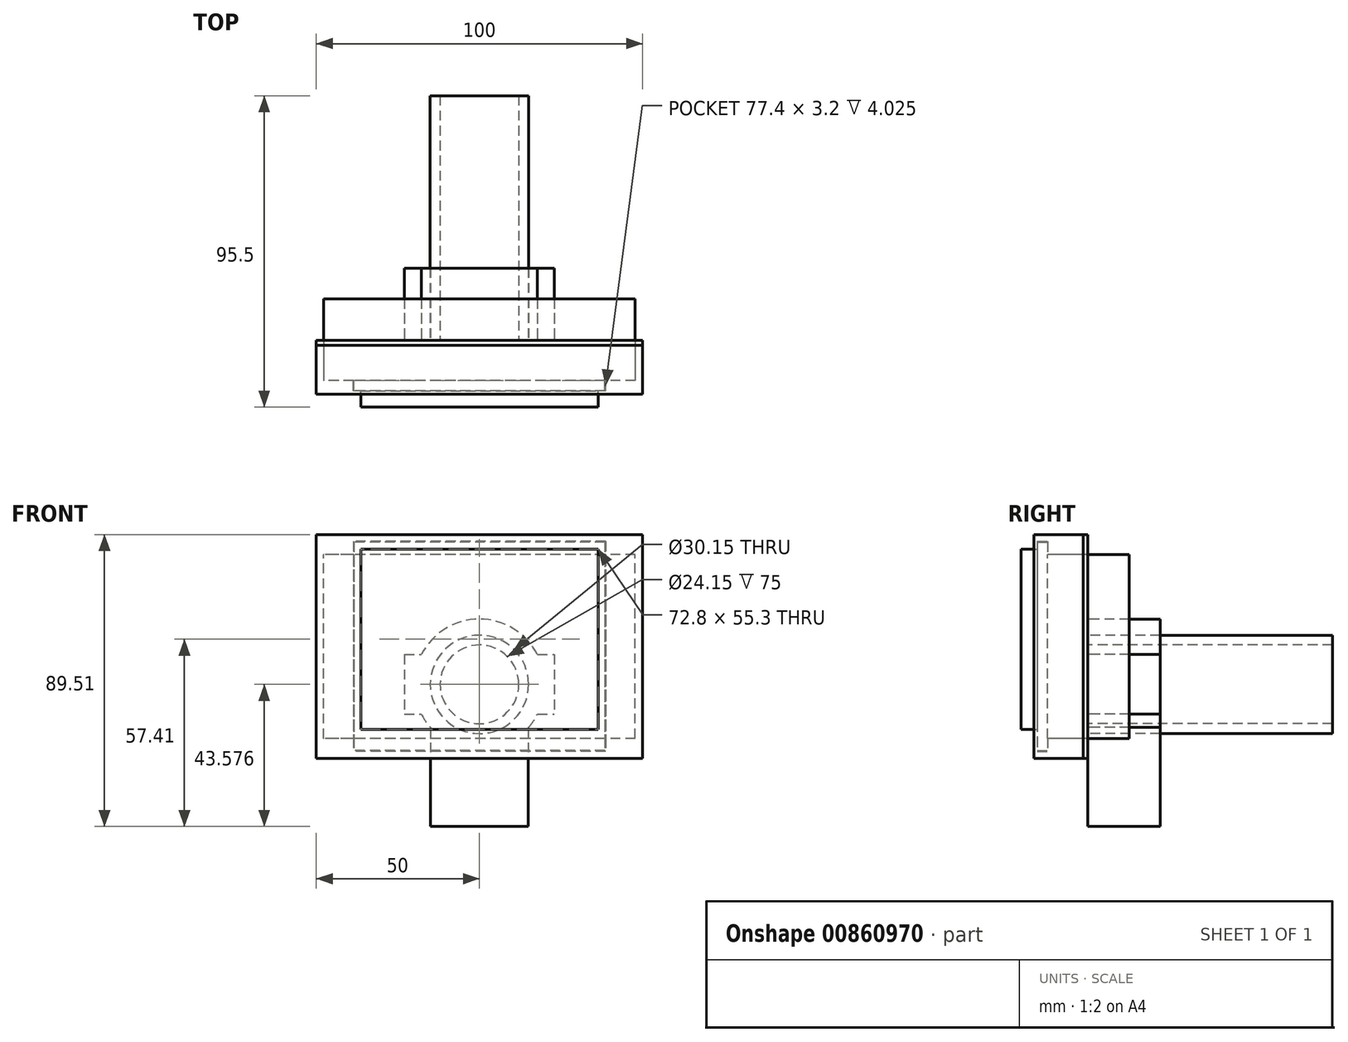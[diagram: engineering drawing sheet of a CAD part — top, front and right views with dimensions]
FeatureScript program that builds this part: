
annotation { "Feature Type Name" : "Feature", "Feature Type Description" : "" }
export const myFeature = defineFeature(function(context is Context, id is Id, definition is map)
    precondition{}
    {
        {
            var Q0;
            Q0=qCreatedBy(makeId("Front.planeOp"),FACE);
            var sketch = newSketch(context, id + "F0", { "sketchPlane" : qUnion([Q0])});
            skLineSegment(sketch, "E0.bottom", {"start": v(38.45, 31.95) * mm, "end": v(-38.45, 31.95) * mm});
            skLineSegment(sketch, "E0.top", {"start": v(38.45, -31.95) * mm, "end": v(-38.45, -31.95) * mm});
            skLineSegment(sketch, "E0.left", {"start": v(38.45, 31.95) * mm, "end": v(38.45, -31.95) * mm});
            skLineSegment(sketch, "E0.right", {"start": v(-38.45, 31.95) * mm, "end": v(-38.45, -31.95) * mm});
            skPoint(sketch, "E0.middle", {"position": v(0, 0) * mm});
            skSolve(sketch);
        }
        {
            var Q0;
            Q0=makeQuery(id+"F0.imprint","IMPRINT",FACE,{"disambiguationData":[TD([[makeQuery(id+"F0.imprint","IMPRINT",EDGE,{"derivedFrom":sQuery(id+"F0.wireOp",EDGE,"E0.bottom")}),1.0]])]});
            extrude(context, id + "F1", {"entities" : qUnion([Q0]), "depth" : 3.2 * mm, "offsetDistance" : 25 * mm});
        }
        {
            var Q0;
            Q0=makeQuery(id+"F1.opExtrude","CAP_FACE",FACE,{"disambiguationData":[OSD([sQuery(id+"F0.wireOp",EDGE,"E0.bottom"),sQuery(id+"F0.wireOp",EDGE,"E0.top"),sQuery(id+"F0.wireOp",EDGE,"E0.left"),sQuery(id+"F0.wireOp",EDGE,"E0.right")])],"isStart":false});
            var sketch = newSketch(context, id + "F2", { "sketchPlane" : qUnion([Q0])});
            skLineSegment(sketch, "E1.bottom", {"start": v(-36.4, 29.85) * mm, "end": v(36.4, 29.85) * mm});
            skLineSegment(sketch, "E1.top", {"start": v(-36.4, -25.45) * mm, "end": v(36.4, -25.45) * mm});
            skLineSegment(sketch, "E1.left", {"start": v(-36.4, 29.85) * mm, "end": v(-36.4, -25.45) * mm});
            skLineSegment(sketch, "E1.right", {"start": v(36.4, 29.85) * mm, "end": v(36.4, -25.45) * mm});
            skLineSegment(sketch, "E2", {"start": v(-38.45, 0) * mm, "end": v(-36.4, 0) * mm, "construction": true});
            skLineSegment(sketch, "E3", {"start": v(38.45, 0) * mm, "end": v(36.4, 0) * mm, "construction": true});
            skSolve(sketch);
        }
        {
            var Q0;
            Q0=makeQuery(id+"F2.imprint","IMPRINT",FACE,{"disambiguationData":[TD([[makeQuery(id+"F2.imprint","IMPRINT",EDGE,{"derivedFrom":sQuery(id+"F2.wireOp",EDGE,"E1.bottom")}),-1.0]])]});
            extrude(context, id + "F3", {"entities" : qUnion([Q0]), "operationType" : NewBodyOperationType.ADD, "depth" : 5 * mm, "offsetDistance" : 25 * mm});
        }
        {
            var Q0;
            Q0=makeQuery(id+"F1.opExtrude","CAP_FACE",FACE,{"disambiguationData":[OSD([sQuery(id+"F0.wireOp",EDGE,"E0.bottom"),sQuery(id+"F0.wireOp",EDGE,"E0.top"),sQuery(id+"F0.wireOp",EDGE,"E0.left"),sQuery(id+"F0.wireOp",EDGE,"E0.right")])],"isStart":true});
            var sketch = newSketch(context, id + "F4", { "sketchPlane" : qUnion([Q0])});
            skLineSegment(sketch, "E4.bottom", {"start": v(-47.77, -28.18) * mm, "end": v(47.77, -28.18) * mm});
            skLineSegment(sketch, "E4.top", {"start": v(-47.77, 28.18) * mm, "end": v(47.77, 28.18) * mm});
            skLineSegment(sketch, "E4.left", {"start": v(-47.77, -28.18) * mm, "end": v(-47.77, 28.18) * mm});
            skLineSegment(sketch, "E4.right", {"start": v(47.77, -28.18) * mm, "end": v(47.77, 28.18) * mm});
            skPoint(sketch, "E4.middle", {"position": v(0, 0) * mm});
            skSolve(sketch);
        }
        {
            var Q0;
            {var subQ0=sQuery(id+"F4.wireOp",EDGE,"E4.left");Q0=makeQuery(id+"F4.imprint","IMPRINT",FACE,{"disambiguationData":[TD([[makeQuery(id+"F4.imprint","IMPRINT",EDGE,{"derivedFrom":subQ0}),1.0]])]});}
            var Q1;
            {var subQ0=sQuery(id+"F4.wireOp",EDGE,"E4.left");Q1=makeQuery(id+"F4.imprint","IMPRINT",FACE,{"disambiguationData":[TD([[makeQuery(id+"F4.imprint","IMPRINT",EDGE,{"derivedFrom":subQ0}),-1.0]])]});}
            var Q2;
            {var subQ0=sQuery(id+"F4.wireOp",EDGE,"E4.bottom");var subQ1=makeQuery(id+"F1.opExtrude","CAP_EDGE",EDGE,{"disambiguationData":[OSD([sQuery(id+"F0.wireOp",EDGE,"E0.right")])],"isStart":true});var subQ2=makeQuery(id+"F4.imprint","INTERSECT",VERTEX,{"derivedFrom":[subQ1,subQ0]});Q2=makeQuery(id+"F4.imprint","IMPRINT",FACE,{"disambiguationData":[TD([[makeQuery(id+"F4.imprint","IMPRINT",EDGE,{"disambiguationData":[TD([[subQ2,-1.0]])],"derivedFrom":subQ0}),1.0]])]});}
            var Q3;
            {var subQ0=sQuery(id+"F4.wireOp",EDGE,"E4.right");Q3=makeQuery(id+"F4.imprint","IMPRINT",FACE,{"disambiguationData":[TD([[makeQuery(id+"F4.imprint","IMPRINT",EDGE,{"derivedFrom":subQ0}),1.0]])]});}
            var Q4;
            {var subQ0=sQuery(id+"F4.wireOp",EDGE,"E4.bottom");var subQ1=makeQuery(id+"F1.opExtrude","CAP_EDGE",EDGE,{"disambiguationData":[OSD([sQuery(id+"F0.wireOp",EDGE,"E0.left")])],"isStart":true});var subQ2=makeQuery(id+"F4.imprint","INTERSECT",VERTEX,{"derivedFrom":[subQ1,subQ0]});Q4=makeQuery(id+"F4.imprint","IMPRINT",FACE,{"disambiguationData":[TD([[makeQuery(id+"F4.imprint","IMPRINT",EDGE,{"disambiguationData":[TD([[subQ2,-1.0]])],"derivedFrom":subQ0}),1.0]])]});}
            extrude(context, id + "F5", {"entities" : qUnion([Q0, Q1, Q2, Q3, Q4]), "operationType" : NewBodyOperationType.ADD, "depth" : 25 * mm, "offsetDistance" : 25 * mm});
        }
        {
            var Q0;
            Q0=makeQuery(id+"F1.opExtrude","CAP_FACE",FACE,{"disambiguationData":[OSD([sQuery(id+"F0.wireOp",EDGE,"E0.bottom"),sQuery(id+"F0.wireOp",EDGE,"E0.top"),sQuery(id+"F0.wireOp",EDGE,"E0.left"),sQuery(id+"F0.wireOp",EDGE,"E0.right")])],"isStart":false});
            cPlane(context, id + "F6", {"entities" : qUnion([Q0]), "cplaneType" : CPlaneType.OFFSET, "offset" : 1 * mm, "width" : 150 * mm, "height" : 150 * mm});
        }
        {
            var Q0;
            Q0=qCreatedBy(id+"F6.planeOp",FACE);
            var sketch = newSketch(context, id + "F7", { "sketchPlane" : qUnion([Q0])});
            skLineSegment(sketch, "E5.bottom", {"start": v(50, 34.3) * mm, "end": v(-50, 34.3) * mm});
            skLineSegment(sketch, "E5.top", {"start": v(50, -34.3) * mm, "end": v(-50, -34.3) * mm});
            skLineSegment(sketch, "E5.left", {"start": v(50, 34.3) * mm, "end": v(50, -34.3) * mm});
            skLineSegment(sketch, "E5.right", {"start": v(-50, 34.3) * mm, "end": v(-50, -34.3) * mm});
            skPoint(sketch, "E5.middle", {"position": v(0, 0) * mm});
            skSolve(sketch);
        }
        {
            var Q0;
            Q0 = qSketchRegion(id + "F7", true);
            extrude(context, id + "F8", {"entities" : qUnion([Q0]), "oppositeDirection" : true, "depth" : 15 * mm, "offsetDistance" : 25 * mm});
        }
        {
            var Q0;
            Q0=makeQuery(id+"F8.opExtrude","CAP_FACE",FACE,{"disambiguationData":[OSD([sQuery(id+"F7.wireOp",EDGE,"E5.bottom"),sQuery(id+"F7.wireOp",EDGE,"E5.top"),sQuery(id+"F7.wireOp",EDGE,"E5.left"),sQuery(id+"F7.wireOp",EDGE,"E5.right")])],"isStart":false});
            extrude(context, id + "F9", {"entities" : qUnion([Q0]), "depth" : 1.5 * mm, "offsetDistance" : 25 * mm});
        }
        {
            var Q0;
            Q0=makeQuery(id+"F1.opExtrude","SWEPT_BODY",BODY,{"disambiguationData":[OSD([sQuery(id+"F0.wireOp",EDGE,"E0.bottom"),sQuery(id+"F0.wireOp",EDGE,"E0.top"),sQuery(id+"F0.wireOp",EDGE,"E0.left"),sQuery(id+"F0.wireOp",EDGE,"E0.right")])]});
            var Q1;
            Q1=makeQuery(id+"F8.opExtrude","SWEPT_BODY",BODY,{"disambiguationData":[OSD([sQuery(id+"F7.wireOp",EDGE,"E5.bottom"),sQuery(id+"F7.wireOp",EDGE,"E5.top"),sQuery(id+"F7.wireOp",EDGE,"E5.left"),sQuery(id+"F7.wireOp",EDGE,"E5.right")])]});
            var Q2;
            Q2=makeQuery(id+"F1.opExtrude","SWEPT_FACE",FACE,{"disambiguationData":[OSD([sQuery(id+"F0.wireOp",EDGE,"E0.top")])]});
            var Q3;
            Q3=makeQuery(id+"F1.opExtrude","SWEPT_FACE",FACE,{"disambiguationData":[OSD([sQuery(id+"F0.wireOp",EDGE,"E0.left")])]});
            var Q4;
            Q4=makeQuery(id+"F1.opExtrude","SWEPT_FACE",FACE,{"disambiguationData":[OSD([sQuery(id+"F0.wireOp",EDGE,"E0.right")])]});
            var Q5;
            Q5=makeQuery(id+"F1.opExtrude","SWEPT_FACE",FACE,{"disambiguationData":[OSD([sQuery(id+"F0.wireOp",EDGE,"E0.bottom")])]});
            var Q6;
            Q6=makeQuery(id+"FdScMa4WtSQwCuE_1.opExtrude","CAP_FACE",FACE,{"disambiguationData":[OSD([sQuery(id+"F4.wireOp",EDGE,"E4.bottom"),sQuery(id+"F4.wireOp",EDGE,"E4.top"),sQuery(id+"F4.wireOp",EDGE,"E4.left"),sQuery(id+"F4.wireOp",EDGE,"E4.right"),sQuery(id+"F4.wireOp",EDGE,"luTbeYwW-3UXa-YMkj-VKAj-5nEcvaAgoGee"),sQuery(id+"F4.wireOp",EDGE,"I1ZiDxWv-xvyy-iAJu-thrK-6Hyi36QBO0zq"),sQuery(id+"F4.wireOp",EDGE,"P3ObkIge-IbjN-rQyK-dse4-T6vLV7bnET73"),sQuery(id+"F4.wireOp",EDGE,"0kIQZrbD-mip6-U8BA-Gkdo-JEn6APyrJIi4"),sQuery(id+"F4.wireOp",EDGE,"AxJcWoIZ-vPJz-4o9D-OFHT-tRSOvJA89BFy")])],"isStart":false});
            var Q7;
            Q7=makeQuery(id+"Fg6QbKwEQV3rp3A_1.opExtrude","SWEPT_FACE",FACE,{"disambiguationData":[OSD([sQuery(id+"FrFVhzk7wVbsbIl_1.wireOp",EDGE,"koiAV4iP-NrPV-3Erd-1VqN-G3aSaU1Oceyf.left")])]});
            var Q8;
            Q8=makeQuery(id+"Fg6QbKwEQV3rp3A_1.boolean.opBoolean","MERGE",FACE,{"derivedFrom":[makeQuery(id+"FdScMa4WtSQwCuE_1.opExtrude","SWEPT_FACE",FACE,{"disambiguationData":[OSD([sQuery(id+"F4.wireOp",EDGE,"E4.top")])]}),makeQuery(id+"Fg6QbKwEQV3rp3A_1.opExtrude","SWEPT_FACE",FACE,{"disambiguationData":[OSD([sQuery(id+"FrFVhzk7wVbsbIl_1.wireOp",EDGE,"koiAV4iP-NrPV-3Erd-1VqN-G3aSaU1Oceyf.bottom")])]})]});
            var Q9;
            Q9=makeQuery(id+"Fg6QbKwEQV3rp3A_1.opExtrude","SWEPT_FACE",FACE,{"disambiguationData":[OSD([sQuery(id+"FrFVhzk7wVbsbIl_1.wireOp",EDGE,"koiAV4iP-NrPV-3Erd-1VqN-G3aSaU1Oceyf.right")])]});
            var Q10;
            Q10=makeQuery(id+"Fg6QbKwEQV3rp3A_1.opExtrude","SWEPT_FACE",FACE,{"disambiguationData":[OSD([sQuery(id+"FrFVhzk7wVbsbIl_1.wireOp",EDGE,"koiAV4iP-NrPV-3Erd-1VqN-G3aSaU1Oceyf.top")])]});
            var Q11;
            Q11=makeQuery(id+"Fg6QbKwEQV3rp3A_1.boolean.opBoolean","MERGE",FACE,{"derivedFrom":[makeQuery(id+"FdScMa4WtSQwCuE_1.opExtrude","SWEPT_FACE",FACE,{"disambiguationData":[OSD([sQuery(id+"F4.wireOp",EDGE,"E4.bottom")])]}),makeQuery(id+"Fg6QbKwEQV3rp3A_1.opExtrude","SWEPT_FACE",FACE,{"disambiguationData":[OSD([sQuery(id+"FrFVhzk7wVbsbIl_1.wireOp",EDGE,"trCcQivb-XzAe-HZob-5Hql-z1Cob8fRHjtp.bottom")])]})]});
            var Q12;
            Q12=makeQuery(id+"Fg6QbKwEQV3rp3A_1.boolean.opBoolean","MERGE",FACE,{"derivedFrom":[makeQuery(id+"FdScMa4WtSQwCuE_1.opExtrude","SWEPT_FACE",FACE,{"disambiguationData":[OSD([sQuery(id+"F4.wireOp",EDGE,"E4.right")])]}),makeQuery(id+"Fg6QbKwEQV3rp3A_1.opExtrude","SWEPT_FACE",FACE,{"disambiguationData":[OSD([sQuery(id+"FrFVhzk7wVbsbIl_1.wireOp",EDGE,"trCcQivb-XzAe-HZob-5Hql-z1Cob8fRHjtp.left")])]})]});
            var Q13;
            Q13=makeQuery(id+"Fg6QbKwEQV3rp3A_1.opExtrude","SWEPT_FACE",FACE,{"disambiguationData":[OSD([sQuery(id+"FrFVhzk7wVbsbIl_1.wireOp",EDGE,"trCcQivb-XzAe-HZob-5Hql-z1Cob8fRHjtp.top")])]});
            var Q14;
            Q14=makeQuery(id+"Fg6QbKwEQV3rp3A_1.opExtrude","SWEPT_FACE",FACE,{"disambiguationData":[OSD([sQuery(id+"FrFVhzk7wVbsbIl_1.wireOp",EDGE,"trCcQivb-XzAe-HZob-5Hql-z1Cob8fRHjtp.right")])]});
            var Q15;
            Q15=makeQuery(id+"Fg6QbKwEQV3rp3A_1.opExtrude","CAP_FACE",FACE,{"disambiguationData":[OSD([sQuery(id+"F4.wireOp",EDGE,"luTbeYwW-3UXa-YMkj-VKAj-5nEcvaAgoGee"),sQuery(id+"F4.wireOp",EDGE,"I1ZiDxWv-xvyy-iAJu-thrK-6Hyi36QBO0zq"),sQuery(id+"F4.wireOp",EDGE,"P3ObkIge-IbjN-rQyK-dse4-T6vLV7bnET73"),sQuery(id+"FrFVhzk7wVbsbIl_1.wireOp",EDGE,"trCcQivb-XzAe-HZob-5Hql-z1Cob8fRHjtp.bottom"),sQuery(id+"FrFVhzk7wVbsbIl_1.wireOp",EDGE,"trCcQivb-XzAe-HZob-5Hql-z1Cob8fRHjtp.top"),sQuery(id+"FrFVhzk7wVbsbIl_1.wireOp",EDGE,"trCcQivb-XzAe-HZob-5Hql-z1Cob8fRHjtp.left"),sQuery(id+"FrFVhzk7wVbsbIl_1.wireOp",EDGE,"trCcQivb-XzAe-HZob-5Hql-z1Cob8fRHjtp.right")])],"isStart":false});
            booleanBodies(context, id + "F10", {"operationType" : BooleanOperationType.SUBTRACTION, "tools" : qUnion([Q0]), "targets" : qUnion([Q1]), "offset" : true, "entitiesToOffset" : qUnion([Q2, Q3, Q4, Q5, Q6, Q7, Q8, Q9, Q10, Q11, Q12, Q13, Q14, Q15]), "offsetDistance" : .25 * mm, "keepTools" : true});
        }
        {
            var Q0;
            Q0=makeQuery(id+"F9.opExtrude","CAP_FACE",FACE,{"disambiguationData":[OSD([sQuery(id+"F7.wireOp",EDGE,"E5.bottom"),sQuery(id+"F7.wireOp",EDGE,"E5.top"),sQuery(id+"F7.wireOp",EDGE,"E5.left"),sQuery(id+"F7.wireOp",EDGE,"E5.right")])],"isStart":false});
            var sketch = newSketch(context, id + "F11", { "sketchPlane" : qUnion([Q0])});
            skCircle(sketch, "E6", {"center": v(0, -11.63) * mm, "radius": 15.07 * mm});
            skLineSegment(sketch, "E7.bottom", {"start": v(23, -2.5) * mm, "end": v(-23, -2.5) * mm});
            skLineSegment(sketch, "E7.top", {"start": v(23, -20.76) * mm, "end": v(-23, -20.76) * mm});
            skLineSegment(sketch, "E7.left", {"start": v(23, -2.5) * mm, "end": v(23, -20.76) * mm});
            skLineSegment(sketch, "E7.right", {"start": v(-23, -2.5) * mm, "end": v(-23, -20.76) * mm});
            skCircle(sketch, "E8", {"center": v(0, -11.63) * mm, "radius": 20 * mm});
            skLineSegment(sketch, "E9.bottom", {"start": v(15, -20.76) * mm, "end": v(-15, -20.76) * mm});
            skLineSegment(sketch, "E9.top", {"start": v(15, -55.2) * mm, "end": v(-15, -55.2) * mm});
            skLineSegment(sketch, "E9.left", {"start": v(15, -20.76) * mm, "end": v(15, -55.2) * mm});
            skLineSegment(sketch, "E9.right", {"start": v(-15, -20.76) * mm, "end": v(-15, -55.2) * mm});
            skPoint(sketch, "E9.middle", {"position": v(0, -37.98) * mm});
            skCircle(sketch, "E10", {"center": v(0, -11.63) * mm, "radius": 12.07 * mm});
            skSolve(sketch);
        }
        {
            var Q0;
            Q0=makeQuery(id+"F11.imprint","IMPRINT",FACE,{"disambiguationData":[TD([[makeQuery(id+"F11.imprint","IMPRINT",EDGE,{"derivedFrom":sQuery(id+"F11.wireOp",EDGE,"E6")}),1.0]])]});
            var Q1;
            {var subQ0=sQuery(id+"F11.wireOp",EDGE,"E7.bottom");var subQ1=sQuery(id+"F11.wireOp",EDGE,"E6");var subQ2=makeQuery(id+"F11.imprint","INTERSECT",VERTEX,{"disambiguationData":[OD(0.0)],"derivedFrom":[subQ1,subQ0]});Q1=makeQuery(id+"F11.imprint","IMPRINT",FACE,{"disambiguationData":[TD([[makeQuery(id+"F11.imprint","IMPRINT",EDGE,{"disambiguationData":[TD([[subQ2,1.0]])],"derivedFrom":subQ1}),1.0]])]});}
            var Q2;
            {var subQ0=sQuery(id+"F11.wireOp",EDGE,"E7.top");var subQ1=sQuery(id+"F11.wireOp",EDGE,"E6");var subQ2=makeQuery(id+"F11.imprint","INTERSECT",VERTEX,{"disambiguationData":[OD(0.0)],"derivedFrom":[subQ1,subQ0]});Q2=makeQuery(id+"F11.imprint","IMPRINT",FACE,{"disambiguationData":[TD([[makeQuery(id+"F11.imprint","IMPRINT",EDGE,{"disambiguationData":[TD([[subQ2,-1.0]])],"derivedFrom":subQ1}),1.0]])]});}
            var Q3;
            {var subQ0=sQuery(id+"F11.wireOp",EDGE,"E9.bottom");var subQ1=sQuery(id+"F11.wireOp",EDGE,"E6");var subQ2=makeQuery(id+"F11.imprint","INTERSECT",VERTEX,{"disambiguationData":[OD(0.0)],"derivedFrom":[subQ1,subQ0]});Q3=makeQuery(id+"F11.imprint","IMPRINT",FACE,{"disambiguationData":[TD([[makeQuery(id+"F11.imprint","IMPRINT",EDGE,{"disambiguationData":[TD([[subQ2,-1.0]])],"derivedFrom":subQ1}),1.0]])]});}
            extrude(context, id + "F12", {"entities" : qUnion([Q0, Q1, Q2, Q3]), "depth" : 75 * mm, "offsetDistance" : 25 * mm});
        }
        {
            var Q0;
            {var subQ0=sQuery(id+"F11.wireOp",EDGE,"E7.right");Q0=makeQuery(id+"F11.imprint","IMPRINT",FACE,{"disambiguationData":[TD([[makeQuery(id+"F11.imprint","IMPRINT",EDGE,{"derivedFrom":subQ0}),1.0]])]});}
            var Q1;
            {var subQ0=sQuery(id+"F11.wireOp",EDGE,"E7.bottom");var subQ1=sQuery(id+"F11.wireOp",EDGE,"E6");var subQ2=makeQuery(id+"F11.imprint","INTERSECT",VERTEX,{"disambiguationData":[OD(0.0)],"derivedFrom":[subQ1,subQ0]});Q1=makeQuery(id+"F11.imprint","IMPRINT",FACE,{"disambiguationData":[TD([[makeQuery(id+"F11.imprint","IMPRINT",EDGE,{"disambiguationData":[TD([[subQ2,-1.0]])],"derivedFrom":subQ1}),-1.0]])]});}
            var Q2;
            {var subQ0=sQuery(id+"F11.wireOp",EDGE,"E7.top");var subQ1=sQuery(id+"F11.wireOp",EDGE,"E6");var subQ2=makeQuery(id+"F11.imprint","INTERSECT",VERTEX,{"disambiguationData":[OD(0.0)],"derivedFrom":[subQ1,subQ0]});Q2=makeQuery(id+"F11.imprint","IMPRINT",FACE,{"disambiguationData":[TD([[makeQuery(id+"F11.imprint","IMPRINT",EDGE,{"disambiguationData":[TD([[subQ2,-1.0]])],"derivedFrom":subQ1}),-1.0]])]});}
            var Q3;
            {var subQ0=sQuery(id+"F11.wireOp",EDGE,"E7.bottom");var subQ1=sQuery(id+"F11.wireOp",EDGE,"E6");var subQ2=makeQuery(id+"F11.imprint","INTERSECT",VERTEX,{"disambiguationData":[OD(1.0)],"derivedFrom":[subQ1,subQ0]});Q3=makeQuery(id+"F11.imprint","IMPRINT",FACE,{"disambiguationData":[TD([[makeQuery(id+"F11.imprint","IMPRINT",EDGE,{"disambiguationData":[TD([[subQ2,1.0]])],"derivedFrom":subQ1}),-1.0]])]});}
            var Q4;
            {var subQ0=sQuery(id+"F11.wireOp",EDGE,"E7.left");Q4=makeQuery(id+"F11.imprint","IMPRINT",FACE,{"disambiguationData":[TD([[makeQuery(id+"F11.imprint","IMPRINT",EDGE,{"derivedFrom":subQ0}),-1.0]])]});}
            var Q5;
            {var subQ0=sQuery(id+"F11.wireOp",EDGE,"E7.bottom");var subQ1=sQuery(id+"F11.wireOp",EDGE,"E6");var subQ2=makeQuery(id+"F11.imprint","INTERSECT",VERTEX,{"disambiguationData":[OD(0.0)],"derivedFrom":[subQ1,subQ0]});Q5=makeQuery(id+"F11.imprint","IMPRINT",FACE,{"disambiguationData":[TD([[makeQuery(id+"F11.imprint","IMPRINT",EDGE,{"disambiguationData":[TD([[subQ2,1.0]])],"derivedFrom":subQ1}),-1.0]])]});}
            var Q6;
            {var subQ1=sQuery(id+"F11.wireOp",EDGE,"E9.bottom");var subQ4=sQuery(id+"F11.wireOp",EDGE,"E6");var subQ8=makeQuery(id+"F11.imprint","INTERSECT",VERTEX,{"disambiguationData":[OD(0.0)],"derivedFrom":[subQ4,subQ1]});Q6=makeQuery(id+"F11.imprint","IMPRINT",FACE,{"disambiguationData":[TD([[makeQuery(id+"F11.imprint","IMPRINT",EDGE,{"disambiguationData":[TD([[subQ8,-1.0]])],"derivedFrom":subQ4}),-1.0]])]});}
            var Q7;
            {var subQ0=sQuery(id+"F11.wireOp",EDGE,"E9.top");Q7=makeQuery(id+"F11.imprint","IMPRINT",FACE,{"disambiguationData":[TD([[makeQuery(id+"F11.imprint","IMPRINT",EDGE,{"derivedFrom":subQ0}),-1.0]])]});}
            var Q8;
            {var subQ0=sQuery(id+"F11.wireOp",EDGE,"E9.right");var subQ1=sQuery(id+"F11.wireOp",EDGE,"E8");var subQ2=makeQuery(id+"F11.imprint","INTERSECT",VERTEX,{"derivedFrom":[subQ1,subQ0]});Q8=makeQuery(id+"F11.imprint","IMPRINT",FACE,{"disambiguationData":[TD([[makeQuery(id+"F11.imprint","IMPRINT",EDGE,{"disambiguationData":[TD([[subQ2,-1.0]])],"derivedFrom":subQ1}),-1.0]])]});}
            var Q9;
            {var subQ1=sQuery(id+"F11.wireOp",EDGE,"E7.top");var subQ3=sQuery(id+"F11.wireOp",EDGE,"E8");var subQ4=makeQuery(id+"F11.imprint","INTERSECT",VERTEX,{"disambiguationData":[OD(0.0)],"derivedFrom":[subQ1,subQ3]});Q9=makeQuery(id+"F11.imprint","IMPRINT",FACE,{"disambiguationData":[TD([[makeQuery(id+"F11.imprint","IMPRINT",EDGE,{"disambiguationData":[TD([[subQ4,1.0]])],"derivedFrom":subQ3}),1.0]])]});}
            var Q10;
            {var subQ1=sQuery(id+"F11.wireOp",EDGE,"E7.top");var subQ3=sQuery(id+"F11.wireOp",EDGE,"E8");var subQ4=makeQuery(id+"F11.imprint","INTERSECT",VERTEX,{"disambiguationData":[OD(1.0)],"derivedFrom":[subQ1,subQ3]});Q10=makeQuery(id+"F11.imprint","IMPRINT",FACE,{"disambiguationData":[TD([[makeQuery(id+"F11.imprint","IMPRINT",EDGE,{"disambiguationData":[TD([[subQ4,-1.0]])],"derivedFrom":subQ3}),1.0]])]});}
            extrude(context, id + "F13", {"entities" : qUnion([Q0, Q1, Q2, Q3, Q4, Q5, Q6, Q7, Q8, Q9, Q10]), "depth" : 22.15 * mm, "offsetDistance" : 25 * mm});
        }
    });
